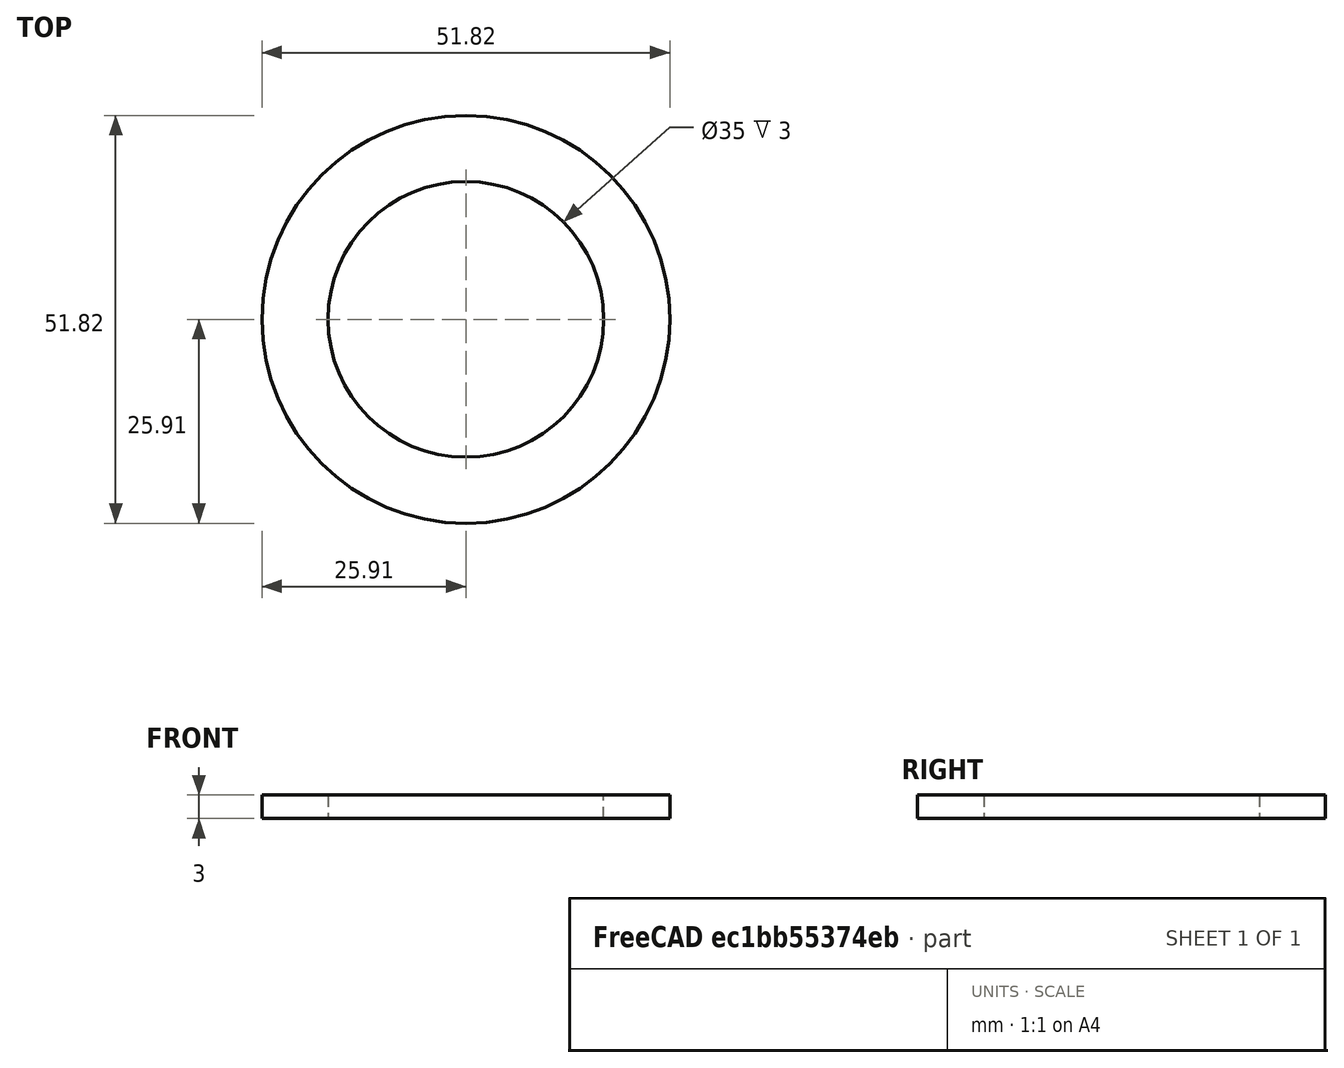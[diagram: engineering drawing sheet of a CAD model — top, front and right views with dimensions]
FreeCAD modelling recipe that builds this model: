
FCSTD DOCUMENT  (FreeCAD 0.20R29177 +426 (Git))
Label: PillowSupportWasher
License: All rights reserved
LicenseURL: http://en.wikipedia.org/wiki/All_rights_reserved
objects: Sketcher::SketchObject×1, PartDesign::Pad×1, PartDesign::Body×1, TechDraw::DrawSVGTemplate×1, TechDraw::DrawViewPart×1, TechDraw::DrawPage×1
note: 4 computed .brp shape members not serialized (recipe doc carries the construction recipe); baked Part::Feature solids carry a one-line shape summary decoded from their .brp

FEATURE [Sketcher::SketchObject] Sketch
  FullyConstrained = true
  MapMode = 5
  Support = -> [XY_Plane]
  sketch-geometry (2):
    g0: Circle CenterX=0 CenterY=0 CenterZ=0 NormalX=0 NormalY=0 NormalZ=1 AngleXU=0 Radius=17.5
    g1: Circle CenterX=0 CenterY=0 CenterZ=0 NormalX=0 NormalY=0 NormalZ=1 AngleXU=0 Radius=25.908
  constraints (4):
    c: Coincident(g0,g-1)
    c: Coincident(g1,g0)
    c: Diameter(g0) = 35
    c: Diameter(g1) = 51.816
FEATURE [PartDesign::Pad] Pad
  Direction = (0,0,1)
  Length = 3
  Length2 = 10
  Profile = -> Sketch
  ReferenceAxis = -> Sketch [N_Axis]
  Type = 0
FEATURE [PartDesign::Body] Body
  Group = -> [Sketch,Pad]
  Origin = -> Origin
  Tip = -> Pad
FEATURE [TechDraw::DrawSVGTemplate] Template
  Height = 841
  Orientation = 1
  Width = 1189
FEATURE [TechDraw::DrawViewPart] View
  CoarseView = false
  Direction = (0,0,1)
  Focus = 100
  HardHidden = false
  IsoCount = 0
  IsoHidden = false
  IsoVisible = false
  LockPosition = false
  Perspective = false
  Rotation = 0
  ScaleType = 0
  SeamHidden = false
  SeamVisible = true
  SmoothHidden = false
  SmoothVisible = true
  Source = -> [Body]
  X = 594.5
  XDirection = (1,0,0)
  Y = 420.5
FEATURE [TechDraw::DrawPage] Page
  KeepUpdated = true
  NextBalloonIndex = 1
  ProjectionType = 0
  Template = -> Template
  Views = -> [View]
